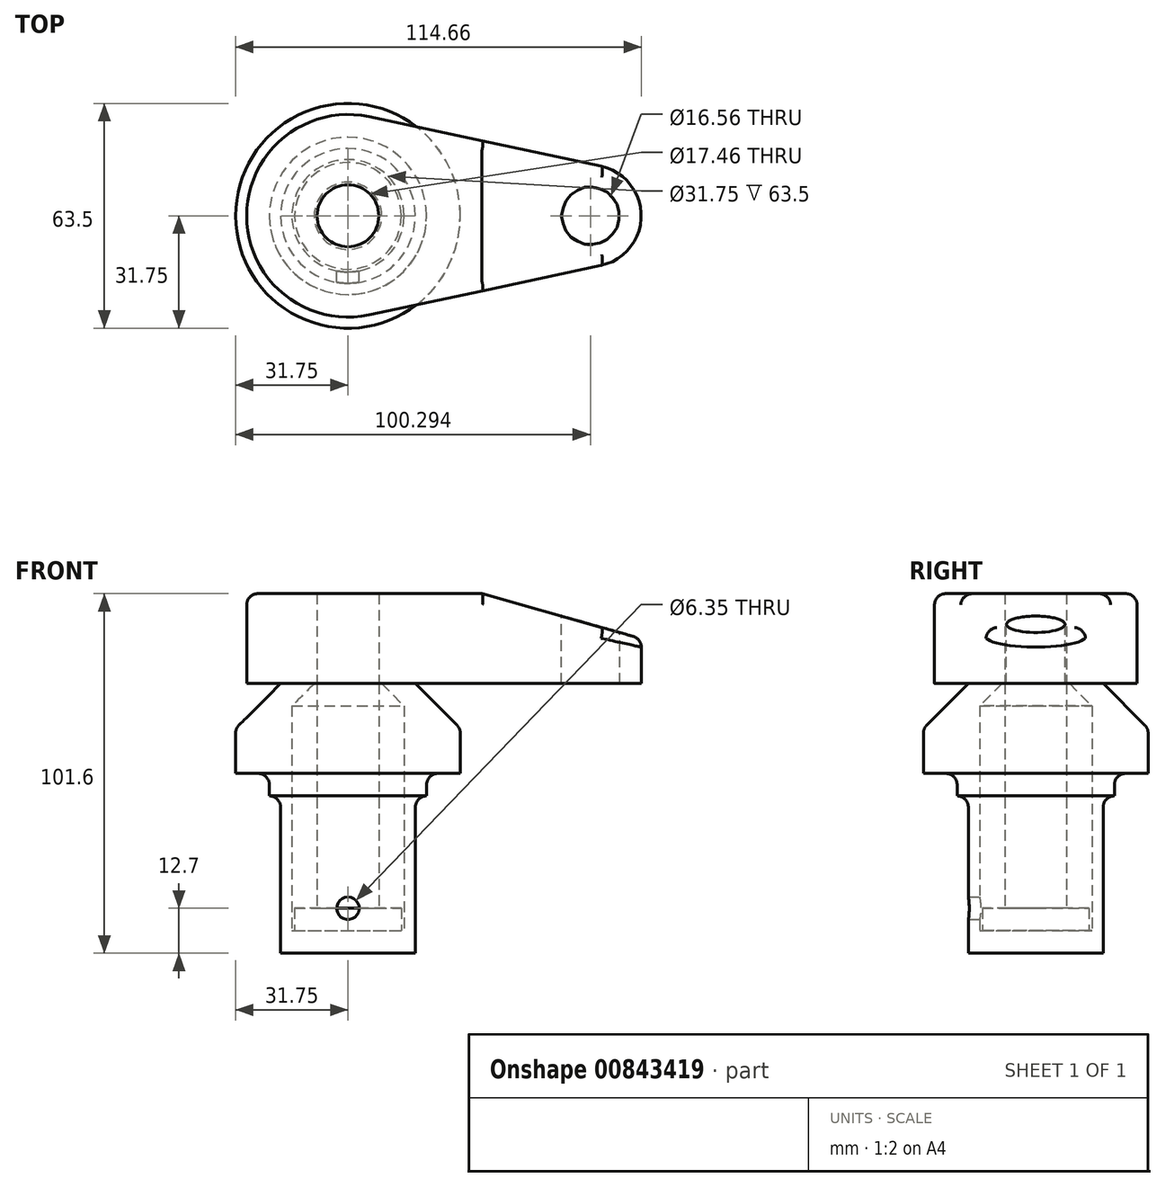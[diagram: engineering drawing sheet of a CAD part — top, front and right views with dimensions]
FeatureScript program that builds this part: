
annotation { "Feature Type Name" : "Feature", "Feature Type Description" : "" }
export const myFeature = defineFeature(function(context is Context, id is Id, definition is map)
    precondition{}
    {
        {
            assignVariable(context, id + "F0", {"name" : "C", "anyValue" : 1 / 812.8 * mm});
        }
        {
            var Q0;
            Q0=qCreatedBy(makeId("Front.planeOp"),FACE);
            var sketch = newSketch(context, id + "F1", { "sketchPlane" : qUnion([Q0])});
            skLineSegment(sketch, "E0", {"start": v(0, 0) * mm, "end": v(0, 76.2) * mm});
            skLineSegment(sketch, "E1", {"start": v(0, 76.2) * mm, "end": v(19.05, 76.2) * mm});
            skLineSegment(sketch, "E2", {"start": v(19.05, 76.2) * mm, "end": v(31.75, 63.5) * mm});
            skLineSegment(sketch, "E3", {"start": v(31.75, 63.5) * mm, "end": v(31.75, 50.8) * mm});
            skLineSegment(sketch, "E4", {"start": v(31.75, 50.8) * mm, "end": v(22.23, 50.8) * mm});
            skLineSegment(sketch, "E5", {"start": v(22.23, 50.8) * mm, "end": v(22.23, 44.45) * mm});
            skLineSegment(sketch, "E6", {"start": v(22.23, 44.45) * mm, "end": v(19.05, 44.45) * mm});
            skLineSegment(sketch, "E7", {"start": v(19.05, 44.45) * mm, "end": v(19.05, 0) * mm});
            skLineSegment(sketch, "E8", {"start": v(9.53, 76.2) * mm, "end": v(15.88, 69.85) * mm});
            skLineSegment(sketch, "E9", {"start": v(15.88, 69.85) * mm, "end": v(15.88, 6.35) * mm});
            skLineSegment(sketch, "E10", {"start": v(0, 6.35) * mm, "end": v(15.88, 6.35) * mm});
            skLineSegment(sketch, "E11", {"start": v(0, 76.2) * mm, "end": v(0, 101.6) * mm});
            skLineSegment(sketch, "E12", {"start": v(0, 101.6) * mm, "end": v(8.73, 101.6) * mm});
            skLineSegment(sketch, "E13", {"start": v(19.05, 0) * mm, "end": v(0, 0) * mm});
            skLineSegment(sketch, "E14", {"start": v(8.73, 101.6) * mm, "end": v(8.73, 12.7) * mm});
            skLineSegment(sketch, "E15", {"start": v(8.73, 12.7) * mm, "end": v(15.08, 12.7) * mm});
            skLineSegment(sketch, "E16", {"start": v(15.08, 12.7) * mm, "end": v(15.08, 6.35) * mm});
            skLineSegment(sketch, "E17", {"start": v(0, 101.6) * mm, "end": v(0, 108.77) * mm, "construction": true});
            skSolve(sketch);
        }
        {
            var Q0;
            {var subQ4=sQuery(id+"F1.wireOp",EDGE,"E2");Q0=makeQuery(id+"F1.imprint","IMPRINT",FACE,{"disambiguationData":[TD([[makeQuery(id+"F1.imprint","IMPRINT",EDGE,{"derivedFrom":subQ4}),-1.0]])]});}
            var Q1;
            {var subQ5=sQuery(id+"F1.wireOp",EDGE,"E10");Q1=makeQuery(id+"F1.imprint","IMPRINT",FACE,{"disambiguationData":[TD([[makeQuery(id+"F1.imprint","IMPRINT",EDGE,{"derivedFrom":subQ5}),-1.0]])]});}
            var Q2;
            Q2=sQuery(id+"F1.wireOp",EDGE,"E0");
            revolve(context, id + "F2", {"surfaceOperationType" : NewSurfaceOperationType.NEW, "entities" : qUnion([Q0, Q1]), "axis" : qUnion([Q2]), "revolveType" : RevolveType.FULL});
        }
        {
            var Q0;
            {var subQ0=sQuery(id+"F1.wireOp",EDGE,"E11");Q0=makeQuery(id+"F1.imprint","IMPRINT",FACE,{"disambiguationData":[TD([[makeQuery(id+"F1.imprint","IMPRINT",EDGE,{"derivedFrom":subQ0}),-1.0]])]});}
            var Q1;
            {var subQ0=sQuery(id+"F1.wireOp",EDGE,"E15");Q1=makeQuery(id+"F1.imprint","IMPRINT",FACE,{"disambiguationData":[TD([[makeQuery(id+"F1.imprint","IMPRINT",EDGE,{"derivedFrom":subQ0}),-1.0]])]});}
            var Q2;
            Q2=sQuery(id+"F1.wireOp",EDGE,"E11");
            revolve(context, id + "F3", {"surfaceOperationType" : NewSurfaceOperationType.NEW, "entities" : qUnion([Q0, Q1]), "axis" : qUnion([Q2]), "revolveType" : RevolveType.FULL});
        }
        {
            var Q0;
            Q0=makeQuery(id+"F3.opRevolve","SWEPT_FACE",FACE,{"disambiguationData":[OSD([sQuery(id+"F1.wireOp",EDGE,"E12")])]});
            var sketch = newSketch(context, id + "F4", { "sketchPlane" : qUnion([Q0])});
            skCircle(sketch, "E18", {"center": v(0, 0) * mm, "radius": 28.62 * mm});
            skCircle(sketch, "E19", {"center": v(68.54, 0) * mm, "radius": 14.37 * mm});
            skLineSegment(sketch, "E20", {"start": v(5.95, 28) * mm, "end": v(71.53, 14.05) * mm});
            skLineSegment(sketch, "E21", {"start": v(5.95, -28) * mm, "end": v(71.53, -14.05) * mm});
            skCircle(sketch, "E22", {"center": v(68.54, 0) * mm, "radius": 8.28 * mm});
            skLineSegment(sketch, "E23", {"start": v(68.54, 0) * mm, "end": v(0, 0) * mm, "construction": true});
            skCircle(sketch, "E24.0", {"center": v(0, 0) * mm, "radius": 8.73 * mm});
            skSolve(sketch);
        }
        {
            var Q0;
            Q0 = qSketchRegion(id + "F4", true);
            var Q1;
            Q1=makeQuery(id+"F2.opRevolve","SWEPT_FACE",FACE,{"disambiguationData":[OSD([sQuery(id+"F1.wireOp",EDGE,"E1")])]});
            extrude(context, id + "F5", {"entities" : qUnion([Q0]), "endBound" : BoundingType.UP_TO_SURFACE, "oppositeDirection" : true, "depth" : 25.4 * mm, "endBoundEntityFace" : qUnion([Q1]), "hasOffset" : true, "offsetDistance" : (getVariable(context, 'C'))});
        }
        {
            var Q0;
            Q0=qCreatedBy(makeId("Front.planeOp"),FACE);
            var sketch = newSketch(context, id + "F6", { "sketchPlane" : qUnion([Q0])});
            skPoint(sketch, "E25", {"position": v(0, 12.7) * mm});
            skSolve(sketch);
        }
        {
            var Q0;
            Q0=sQuery(id+"F6.wireOp",VERTEX,"E25");
            var Q1;
            Q1=makeQuery(id+"F2.opRevolve","SWEPT_BODY",BODY,{"disambiguationData":[OSD([sQuery(id+"F1.wireOp",EDGE,"E0"),sQuery(id+"F1.wireOp",EDGE,"E1"),sQuery(id+"F1.wireOp",EDGE,"E2"),sQuery(id+"F1.wireOp",EDGE,"E3"),sQuery(id+"F1.wireOp",EDGE,"E4"),sQuery(id+"F1.wireOp",EDGE,"E5"),sQuery(id+"F1.wireOp",EDGE,"E6"),sQuery(id+"F1.wireOp",EDGE,"E7"),sQuery(id+"F1.wireOp",EDGE,"E8"),sQuery(id+"F1.wireOp",EDGE,"E9"),sQuery(id+"F1.wireOp",EDGE,"E10"),sQuery(id+"F1.wireOp",EDGE,"E13")])]});
            hole(context, id + "F7", {"style" : HoleStyle.SIMPLE, "endStyle" : HoleEndStyle.THROUGH, "oppositeDirection" : true, "holeDiameter" : 6.35 * mm, "majorDiameter" : 6.35 * mm, "isTappedThrough" : true, "tappedDepth" : 12.7 * mm, "tapClearance" : 3, "locations" : qUnion([Q0]), "scope" : qUnion([Q1])});
        }
        {
            var Q0;
            Q0=qCreatedBy(makeId("Front.planeOp"),FACE);
            var sketch = newSketch(context, id + "F8", { "sketchPlane" : qUnion([Q0])});
            skLineSegment(sketch, "E26", {"start": v(82.91, 88.9) * mm, "end": v(37.8, 101.6) * mm});
            skLineSegment(sketch, "E27", {"start": v(37.8, 101.6) * mm, "end": v(82.91, 101.6) * mm});
            skLineSegment(sketch, "E28", {"start": v(82.91, 101.6) * mm, "end": v(82.91, 88.9) * mm});
            skSolve(sketch);
        }
        {
            var Q0;
            Q0 = qSketchRegion(id + "F8", true);
            extrude(context, id + "F9", {"entities" : qUnion([Q0]), "operationType" : NewBodyOperationType.REMOVE, "endBound" : BoundingType.THROUGH_ALL, "oppositeDirection" : true, "depth" : 25.4 * mm, "offsetDistance" : 25.4 * mm, "hasSecondDirection" : true, "secondDirectionBound" : SecondDirectionBoundingType.THROUGH_ALL, "secondDirectionOppositeDirection" : false, "secondDirectionDepth" : 25.4 * mm});
        }
        {
            var Q0;
            Q0=makeQuery(id+"F9.boolean.opBoolean","COPY",EDGE,{"derivedFrom":makeQuery(id+"F9.opExtrude","SWEPT_EDGE",EDGE,{"disambiguationData":[OSD([sQuery(id+"F8.wireOp",EDGE,"E26"),sQuery(id+"F8.wireOp",EDGE,"E27")])]})});
            var Q1;
            Q1=makeQuery(id+"F9.boolean.opBoolean","INTERSECT",EDGE,{"derivedFrom":[makeQuery(id+"F5.opExtrude","SWEPT_FACE",FACE,{"disambiguationData":[OSD([sQuery(id+"F4.wireOp",EDGE,"E20")])]}),makeQuery(id+"F9.opExtrude","SWEPT_FACE",FACE,{"disambiguationData":[OSD([sQuery(id+"F8.wireOp",EDGE,"E26")])]})]});
            var Q2;
            Q2=makeQuery(id+"F5.opExtrude","CAP_EDGE",EDGE,{"disambiguationData":[OSD([sQuery(id+"F4.wireOp",EDGE,"E20")])],"isStart":true});
            var Q3;
            Q3=makeQuery(id+"F2.opRevolve","SWEPT_EDGE",EDGE,{"disambiguationData":[OSD([sQuery(id+"F1.wireOp",EDGE,"E6"),sQuery(id+"F1.wireOp",EDGE,"E7")])]});
            var Q4;
            Q4=makeQuery(id+"F2.opRevolve","SWEPT_EDGE",EDGE,{"disambiguationData":[OSD([sQuery(id+"F1.wireOp",EDGE,"E4"),sQuery(id+"F1.wireOp",EDGE,"E5")])]});
            var Q5;
            Q5=makeQuery(id+"F2.opRevolve","SWEPT_EDGE",EDGE,{"disambiguationData":[OSD([sQuery(id+"F1.wireOp",EDGE,"E2"),sQuery(id+"F1.wireOp",EDGE,"E3")])]});
            fillet(context, id + "F10", {"entities" : qUnion([Q0, Q1, Q2, Q3, Q4, Q5]), "radius" : 3.17 * mm, "tangentPropagation" : true, "allowEdgeOverflow" : false});
        }
    });
